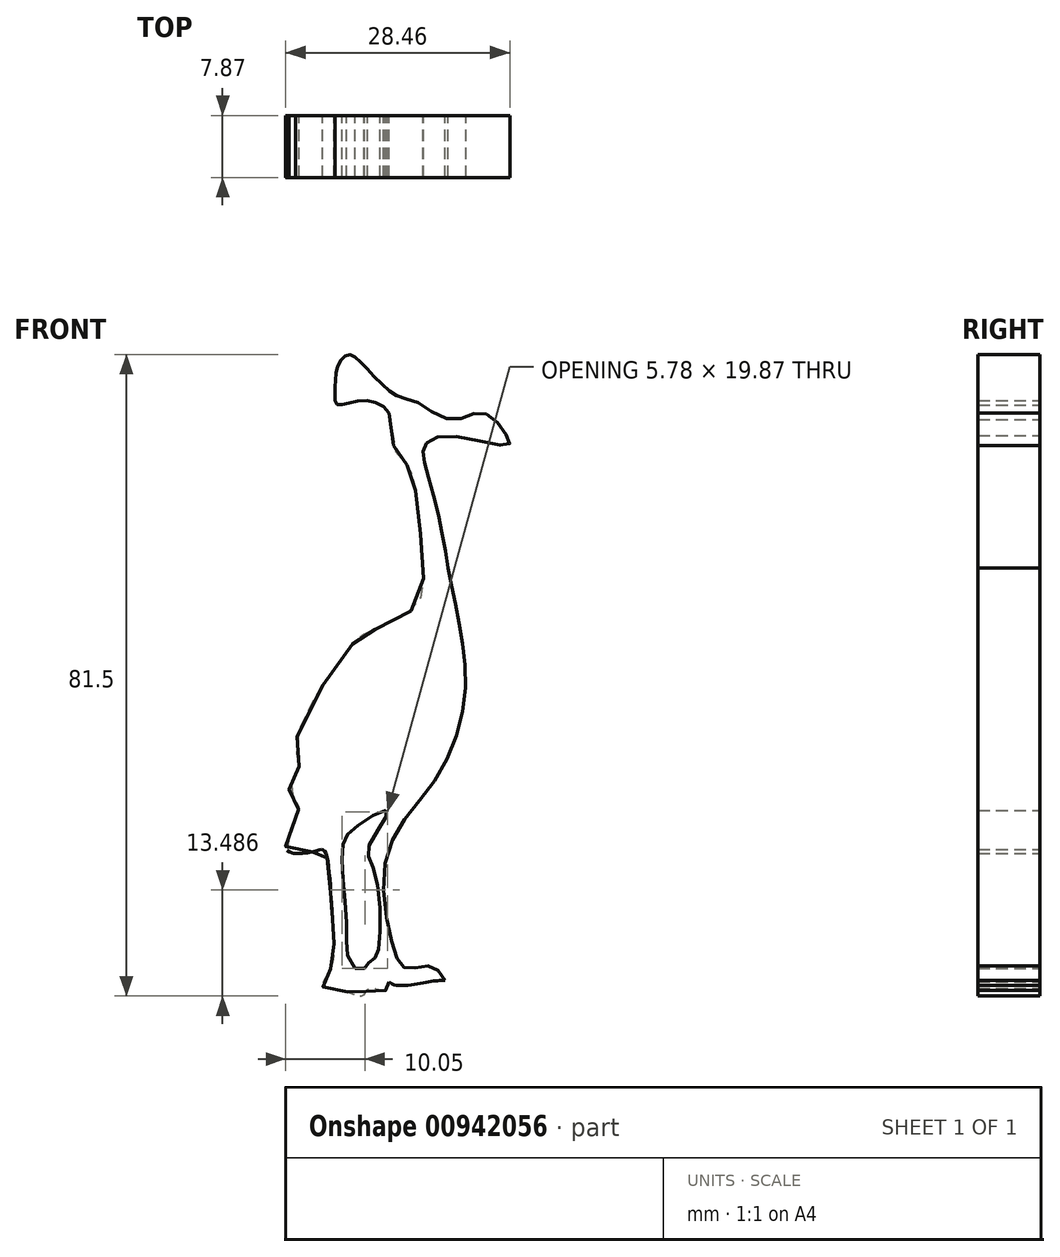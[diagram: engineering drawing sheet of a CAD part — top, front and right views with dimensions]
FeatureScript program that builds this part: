
annotation { "Feature Type Name" : "Feature", "Feature Type Description" : "" }
export const myFeature = defineFeature(function(context is Context, id is Id, definition is map)
    precondition{}
    {
        {
            var Q0;
            Q0=qCreatedBy(makeId("Front.planeOp"),FACE);
            var sketch = newSketch(context, id + "F0", { "sketchPlane" : qUnion([Q0])});
            skFitSpline(sketch, "E0", {"points": [v(-23.43, -24.17) * mm, v(-25.26, -22.35) * mm, v(-28.3, -22.6) * mm, v(-29.88, -20.4) * mm, v(-30.85, -8.24) * mm, v(-24.77, 1.25) * mm, v(-20.88, 12.44) * mm, v(-21.73, 21.56) * mm, v(-23.07, 28.25) * mm], "startDerivative": vector(-19.4, 32.17) * mm, "endDerivative": vector(-10.5, 51.83) * mm});
            skPoint(sketch, "E1.9.internal.snap0", {"position": v(-27.25, 62.38) * mm});
            skPoint(sketch, "E1.20.internal.snap0", {"position": v(-27.25, 62.38) * mm});
            skPoint(sketch, "E1.22.internal.snap0", {"position": v(-27.25, 62.38) * mm});
            skFitSpline(sketch, "E1", {"points": [v(-23.07, 28.25) * mm, v(-24.24, 34.72) * mm, v(-25.99, 41.4) * mm, v(-26.13, 43.59) * mm, v(-23.07, 45.04) * mm, v(-15.37, 43.88) * mm, v(-15.95, 45.62) * mm, v(-18.86, 47.95) * mm, v(-22.63, 47.08) * mm, v(-27.25, 49.4) * mm, v(-29.62, 50.13) * mm, v(-33.84, 54.06) * mm, v(-35.81, 55.34) * mm, v(-37.15, 53.63) * mm, v(-37.4, 50.84) * mm, v(-37.15, 49) * mm, v(-34.35, 49.5) * mm, v(-30.58, 47.91) * mm, v(-29.85, 43.3) * mm, v(-28.27, 41.34) * mm, v(-27.25, 38.42) * mm, v(-26.32, 29.54) * mm, v(-27.25, 23.33) * mm, v(-33.26, 20.05) * mm, v(-35.7, 17.98) * mm, v(-42.38, 6.18) * mm, v(-42.02, 2.65) * mm, v(-43.24, 0) * mm, v(-42.02, -1.61) * mm, v(-43.6, -7.45) * mm, v(-39.83, -7.7) * mm, v(-38.73, -7.7) * mm, v(-37.82, -15.23) * mm, v(-37.6, -21.1) * mm, v(-38.36, -23.37) * mm, v(-39.01, -24.9) * mm, v(-37.06, -25.22) * mm, v(-33.8, -26.09) * mm, v(-33.15, -25.22) * mm, v(-30.98, -25.43) * mm, v(-34.89, -22.6) * mm, v(-35.97, -17.3) * mm, v(-36.52, -7.53) * mm, v(-34.89, -4.7) * mm, v(-30.76, -2.65) * mm, v(-33.15, -7.2) * mm, v(-32.4, -10.35) * mm, v(-31.96, -20.44) * mm, v(-32.83, -21.64) * mm, v(-33.7, -22.6) * mm, v(-31.09, -23.37) * mm, v(-30.55, -24.35) * mm, v(-28.3, -24.78) * mm, v(-25.01, -24.24) * mm, v(-23.43, -24.17) * mm], "startDerivative": vector(-39.6, 253.3) * mm, "endDerivative": vector(119.13, -2.46) * mm});
            skLineSegment(sketch, "E2", {"start": v(-34.89, -22.6) * mm, "end": v(-33.7, -22.6) * mm});
            skLineSegment(sketch, "E3", {"start": v(-29.62, 50.13) * mm, "end": v(-30.58, 47.91) * mm});
            skLineSegment(sketch, "E4", {"start": v(-30.98, -25.43) * mm, "end": v(-30.55, -24.35) * mm});
            skSolve(sketch);
        }
        {
            var Q0;
            Q0 = qSketchRegion(id + "F0", true);
            extrude(context, id + "F1", {"entities" : qUnion([Q0]), "depth" : 7.87 * mm, "offsetDistance" : 25.4 * mm});
        }
    });
